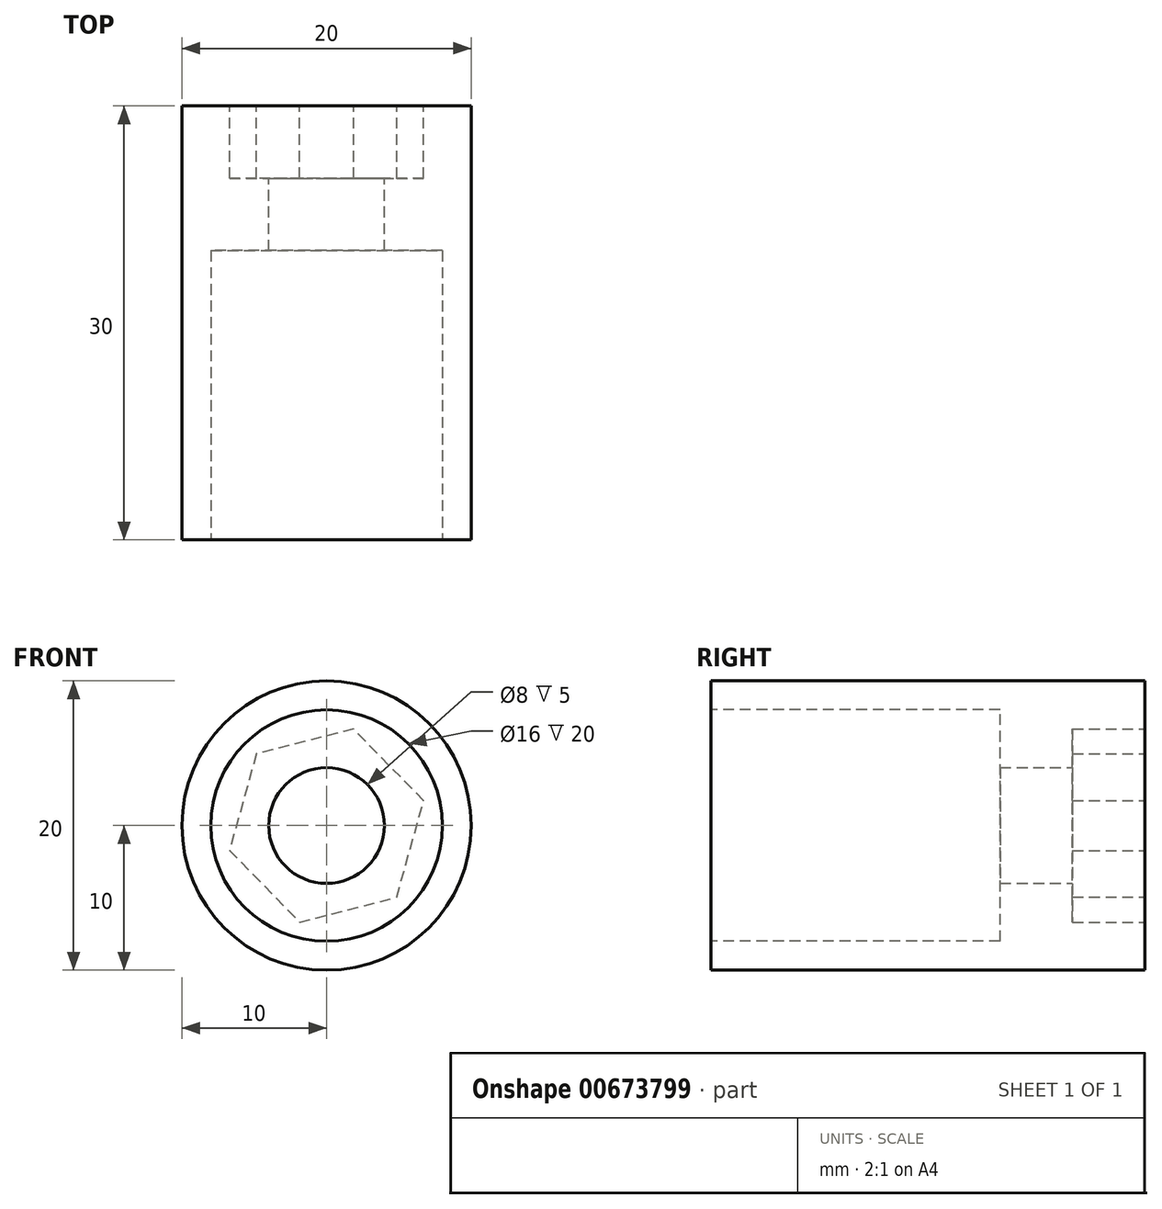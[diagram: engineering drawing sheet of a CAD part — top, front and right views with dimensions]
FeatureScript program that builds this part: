
annotation { "Feature Type Name" : "Feature", "Feature Type Description" : "" }
export const myFeature = defineFeature(function(context is Context, id is Id, definition is map)
    precondition{}
    {
        {
            var Q0;
            Q0=qCreatedBy(makeId("Front.planeOp"),FACE);
            var sketch = newSketch(context, id + "F0", { "sketchPlane" : qUnion([Q0])});
            skCircle(sketch, "E0", {"center": v(0, 0) * mm, "radius": 10 * mm});
            skSolve(sketch);
        }
        {
            var Q0;
            Q0=makeQuery(id+"F0.imprint","IMPRINT",FACE,{"disambiguationData":[TD([[makeQuery(id+"F0.imprint","IMPRINT",EDGE,{"derivedFrom":sQuery(id+"F0.wireOp",EDGE,"E0")}),1.0]])]});
            extrude(context, id + "F1", {"entities" : qUnion([Q0]), "depth" : 30 * mm, "offsetDistance" : 25 * mm});
        }
        {
            var Q0;
            Q0=makeQuery(id+"F1.opExtrude","CAP_FACE",FACE,{"disambiguationData":[OSD([sQuery(id+"F0.wireOp",EDGE,"E0")])],"isStart":false});
            var sketch = newSketch(context, id + "F2", { "sketchPlane" : qUnion([Q0])});
            skCircle(sketch, "E1", {"center": v(0, 0) * mm, "radius": 8 * mm});
            skSolve(sketch);
        }
        {
            var Q0;
            Q0=makeQuery(id+"F2.imprint","IMPRINT",FACE,{"disambiguationData":[TD([[makeQuery(id+"F2.imprint","IMPRINT",EDGE,{"derivedFrom":sQuery(id+"F2.wireOp",EDGE,"E1")}),1.0]])]});
            extrude(context, id + "F3", {"entities" : qUnion([Q0]), "operationType" : NewBodyOperationType.REMOVE, "oppositeDirection" : true, "depth" : 20 * mm, "offsetDistance" : 25 * mm});
        }
        {
            var Q0;
            Q0=makeQuery(id+"F1.opExtrude","CAP_FACE",FACE,{"disambiguationData":[OSD([sQuery(id+"F0.wireOp",EDGE,"E0")])],"isStart":true});
            var sketch = newSketch(context, id + "F4", { "sketchPlane" : qUnion([Q0])});
            skCircle(sketch, "E2", {"center": v(0, 0) * mm, "radius": 4 * mm});
            skSolve(sketch);
        }
        {
            var Q0;
            Q0=makeQuery(id+"F4.imprint","IMPRINT",FACE,{"disambiguationData":[TD([[makeQuery(id+"F4.imprint","IMPRINT",EDGE,{"derivedFrom":sQuery(id+"F4.wireOp",EDGE,"E2")}),1.0]])]});
            extrude(context, id + "F5", {"entities" : qUnion([Q0]), "operationType" : NewBodyOperationType.REMOVE, "endBound" : BoundingType.THROUGH_ALL, "oppositeDirection" : true, "depth" : 25 * mm, "offsetDistance" : 25 * mm});
        }
        {
            var Q0;
            Q0=makeQuery(id+"F1.opExtrude","CAP_FACE",FACE,{"disambiguationData":[OSD([sQuery(id+"F0.wireOp",EDGE,"E0")])],"isStart":true});
            var sketch = newSketch(context, id + "F6", { "sketchPlane" : qUnion([Q0])});
            skCircle(sketch, "E3.cCircle", {"center": v(0, 0) * mm, "radius": 6 * mm, "construction": true});
            skLineSegment(sketch, "E3.0", {"start": v(-1.86, 6.67) * mm, "end": v(4.85, 4.95) * mm});
            skLineSegment(sketch, "E3.1", {"start": v(4.85, 4.95) * mm, "end": v(6.71, -1.72) * mm});
            skLineSegment(sketch, "E3.2", {"start": v(6.71, -1.72) * mm, "end": v(1.86, -6.67) * mm});
            skLineSegment(sketch, "E3.3", {"start": v(1.86, -6.67) * mm, "end": v(-4.85, -4.95) * mm});
            skLineSegment(sketch, "E3.4", {"start": v(-4.85, -4.95) * mm, "end": v(-6.71, 1.72) * mm});
            skLineSegment(sketch, "E3.5", {"start": v(-6.71, 1.72) * mm, "end": v(-1.86, 6.67) * mm});
            skPoint(sketch, "E3.0.midPoint", {"position": v(1.5, 5.81) * mm});
            skSolve(sketch);
        }
        {
            var Q0;
            Q0=makeQuery(id+"F6.imprint","IMPRINT",FACE,{"disambiguationData":[TD([[makeQuery(id+"F6.imprint","IMPRINT",EDGE,{"derivedFrom":sQuery(id+"F6.wireOp",EDGE,"E3.0")}),-1.0]])]});
            extrude(context, id + "F7", {"entities" : qUnion([Q0]), "operationType" : NewBodyOperationType.REMOVE, "oppositeDirection" : true, "depth" : 5 * mm, "offsetDistance" : 25 * mm});
        }
    });
